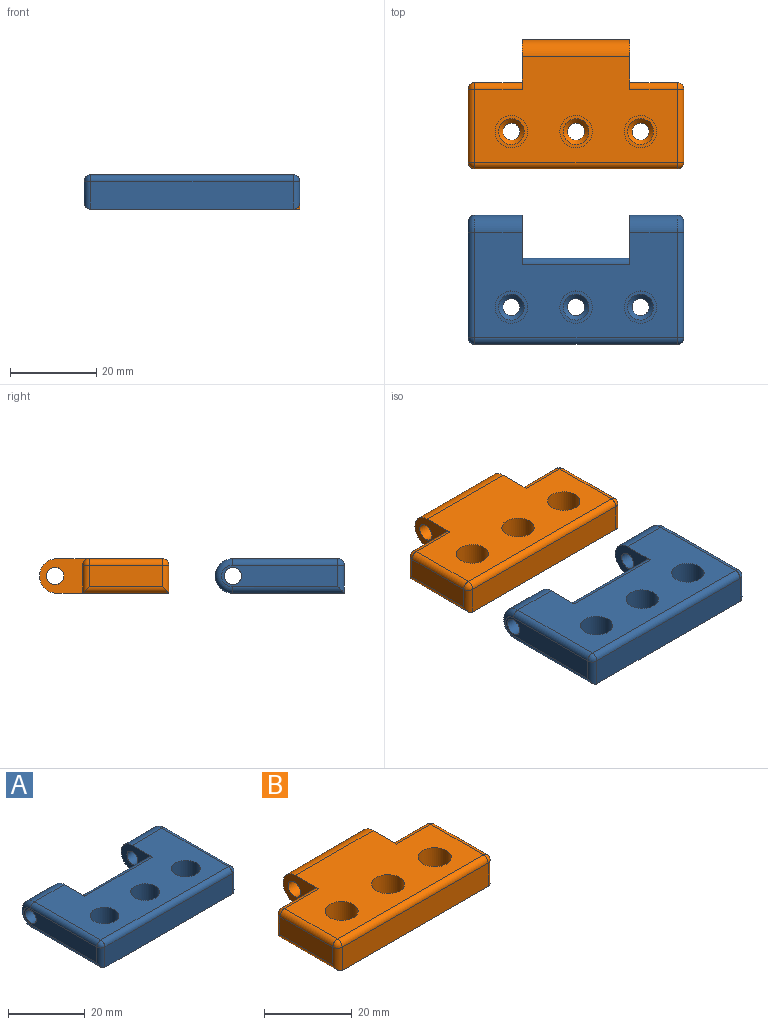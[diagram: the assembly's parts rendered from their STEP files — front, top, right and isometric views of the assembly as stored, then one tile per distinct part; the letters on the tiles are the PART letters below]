
ASSEMBLY  parts=2 mates=1
PART A: 36 faces, bbox 50x30.3x8.7 mm
  f0: cylinder r=2mm len=4mm, axis (0,0,-1), area 12.6mm2, adj f10,f23
  f1: cylinder r=2mm len=4mm, axis (0,0,-1), area 12.6mm2, adj f10,f25
  f2: cylinder r=2mm len=4mm, axis (0,0,-1), area 12.6mm2, adj f10,f24
  f3: plane 11.5x8mm, normal (1,0,0), area 61mm2, adj f8,f9,f10,f12,f14,f16
  f4: plane 27x5mm, normal (-1,0,0), area 119.8mm2, adj f12,f26,f28,f29,f30
  f5: plane 47x6.5mm, normal (0,-1,0), area 305.5mm2, adj f10,f15,f29,f34
  f6: plane 27x5mm, normal (1,0,0), area 119.8mm2, adj f11,f31,f33,f34,f35
  f7: plane 11.5x8mm, normal (-1,0,0), area 61mm2, adj f8,f9,f10,f11,f13,f16
  f8: plane 25x6.5mm, normal (0,1,0), area 162.5mm2, adj f3,f7,f10,f16
  f9: plane 47x24.5mm, normal (0,0,1), area 831.5mm2, adj f3,f7,f13,f14,f15,f16,f17,f19
  f10: plane 47x26mm, normal (0,0,-1), area 1034.3mm2, adj f0,f1,f2,f3,f5,f7,f8,f13
  f11: cylinder r=2mm len=12.5mm, axis (-1,0,0), area 157.1mm2, adj f6,f7
  f12: cylinder r=2mm len=12.5mm, axis (-1,0,0), area 157.1mm2, adj f3,f4
  f13: cylinder r=4mm len=11mm, axis (1,0,0), area 138.2mm2, adj f7,f9,f10,f33
  f14: cylinder r=4mm len=11mm, axis (1,0,0), area 138.2mm2, adj f3,f9,f10,f28
  f15: cylinder r=1.5mm len=47mm, axis (-1,0,0), area 110.7mm2, adj f5,f9,f27,f32
  f16: cylinder r=1.5mm len=25mm, axis (1,0,0), area 58.9mm2, adj f3,f7,f8,f9
  f17: cylinder r=3.75mm len=7.5mm, axis (0,0,1), area 141.4mm2, adj f9,f18
  f18: plane 7.5x7.5mm, normal (0,0,1), area 15.9mm2, adj f17,f24
  f19: cylinder r=3.75mm len=7.5mm, axis (0,0,1), area 141.4mm2, adj f9,f20
  f20: plane 7.5x7.5mm, normal (0,0,1), area 15.9mm2, adj f19,f25
  f21: cylinder r=3.75mm len=7.5mm, axis (0,0,1), area 141.4mm2, adj f9,f22
  f22: plane 7.5x7.5mm, normal (0,0,1), area 15.9mm2, adj f21,f23
  f23: cone r=2mm half-angle=45deg, axis (0,0,1), area 22.2mm2, adj f0,f22
  f24: cone r=2mm half-angle=45deg, axis (0,0,1), area 22.2mm2, adj f2,f18
  f25: cone r=2mm half-angle=45deg, axis (0,0,1), area 22.2mm2, adj f1,f20
  f26: cylinder r=1.5mm len=24.5mm, axis (0,1,0), area 57.7mm2, adj f4,f9,f27,f28
  f27: sphere r=1.5mm, area 3.5mm2, adj f15,f26,f29
  f28: torus R=2.5mm, axis (1,0,0), area 25.6mm2, adj f4,f14,f26,f30
  f29: cylinder r=1.5mm len=6.5mm, axis (0,0,1), area 14mm2, adj f4,f5,f27,f30
  f30: cylinder r=1.5mm len=26mm, axis (0,-1,0), area 60mm2, adj f4,f10,f28,f29
  f31: cylinder r=1.5mm len=24.5mm, axis (0,-1,0), area 57.7mm2, adj f6,f9,f32,f33
  f32: sphere r=1.5mm, area 3.5mm2, adj f15,f31,f34
  f33: torus R=2.5mm, axis (1,0,0), area 25.6mm2, adj f6,f13,f31,f35
  f34: cylinder r=1.5mm len=6.5mm, axis (0,0,-1), area 14mm2, adj f5,f6,f32,f35
  f35: cylinder r=1.5mm len=26mm, axis (0,1,0), area 60mm2, adj f6,f10,f33,f34
PART B: 37 faces, bbox 50x30x8 mm
  f0: cylinder r=2mm len=4mm, axis (0,0,-1), area 12.6mm2, adj f11,f23
  f1: cylinder r=2mm len=4mm, axis (0,0,-1), area 12.6mm2, adj f11,f25
  f2: cylinder r=2mm len=4mm, axis (0,0,-1), area 12.6mm2, adj f11,f24
  f3: plane 11.5x8mm, normal (-1,0,0), area 61mm2, adj f4,f10,f11,f12,f13,f16
  f4: plane 11x6.5mm, normal (0,1,0), area 71.5mm2, adj f3,f11,f16,f31
  f5: plane 17x5mm, normal (-1,0,0), area 85mm2, adj f31,f32,f34,f35
  f6: plane 47x6.5mm, normal (0,-1,0), area 305.5mm2, adj f11,f15,f26,f34
  f7: plane 17x6.5mm, normal (1,0,0), area 110.5mm2, adj f11,f26,f28,f30
  f8: plane 11x6.5mm, normal (0,1,0), area 71.5mm2, adj f9,f11,f14,f30
  f9: plane 11.5x8mm, normal (1,0,0), area 61mm2, adj f8,f10,f11,f12,f13,f14
  f10: plane 47x24.5mm, normal (0,0,1), area 854mm2, adj f3,f9,f13,f14,f15,f16,f17,f19
  f11: plane 48.5x26mm, normal (0,0,-1), area 1081.3mm2, adj f0,f1,f2,f3,f4,f6,f7,f8
  f12: cylinder r=2mm len=25mm, axis (-1,0,0), area 314.2mm2, adj f3,f9
  f13: cylinder r=4mm len=25mm, axis (1,0,0), area 314.2mm2, adj f3,f9,f10,f11
  f14: cylinder r=1.5mm len=11mm, axis (1,0,0), area 25.9mm2, adj f8,f9,f10,f29
  f15: cylinder r=1.5mm len=47mm, axis (-1,0,0), area 110.7mm2, adj f6,f10,f27,f36
  f16: cylinder r=1.5mm len=11mm, axis (1,0,0), area 25.9mm2, adj f3,f4,f10,f33
  f17: cylinder r=3.75mm len=7.5mm, axis (0,0,1), area 141.4mm2, adj f10,f18
  f18: plane 7.5x7.5mm, normal (0,0,1), area 15.9mm2, adj f17,f23
  f19: cylinder r=3.75mm len=7.5mm, axis (0,0,1), area 141.4mm2, adj f10,f20
  f20: plane 7.5x7.5mm, normal (0,0,1), area 15.9mm2, adj f19,f24
  f21: cylinder r=3.75mm len=7.5mm, axis (0,0,1), area 141.4mm2, adj f10,f22
  f22: plane 7.5x7.5mm, normal (0,0,1), area 15.9mm2, adj f21,f25
  f23: cone r=2mm half-angle=45deg, axis (0,0,1), area 22.2mm2, adj f0,f18
  f24: cone r=2mm half-angle=45deg, axis (0,0,1), area 22.2mm2, adj f2,f20
  f25: cone r=2mm half-angle=45deg, axis (0,0,1), area 22.2mm2, adj f1,f22
  f26: cylinder r=1.5mm len=6.5mm, axis (0,0,-1), area 15.3mm2, adj f6,f7,f11,f27
  f27: sphere r=1.5mm, area 3.5mm2, adj f15,f26,f28
  f28: cylinder r=1.5mm len=17mm, axis (0,-1,0), area 40.1mm2, adj f7,f10,f27,f29
  f29: sphere r=1.5mm, area 3.5mm2, adj f14,f28,f30
  f30: cylinder r=1.5mm len=6.5mm, axis (0,0,-1), area 15.3mm2, adj f7,f8,f11,f29
  f31: cylinder r=1.5mm len=6.5mm, axis (0,0,-1), area 14mm2, adj f4,f5,f32,f33
  f32: cylinder r=1.5mm len=20mm, axis (0,-1,0), area 44.6mm2, adj f5,f11,f31,f34
  f33: sphere r=1.5mm, area 3.5mm2, adj f16,f31,f35
  f34: cylinder r=1.5mm len=6.5mm, axis (0,0,1), area 14mm2, adj f5,f6,f32,f36
  f35: cylinder r=1.5mm len=17mm, axis (0,1,0), area 40.1mm2, adj f5,f10,f33,f36
  f36: sphere r=1.5mm, area 3.5mm2, adj f15,f34,f35
PLACE A t=(12.07,-2.67,8.76)mm
PLACE B t=(12.07,38.09,8.76)mm
MATE pin_slot A.f11 <-> B.f12  axis (1,0,0) through (-0.43,8.21,12.76)mm
